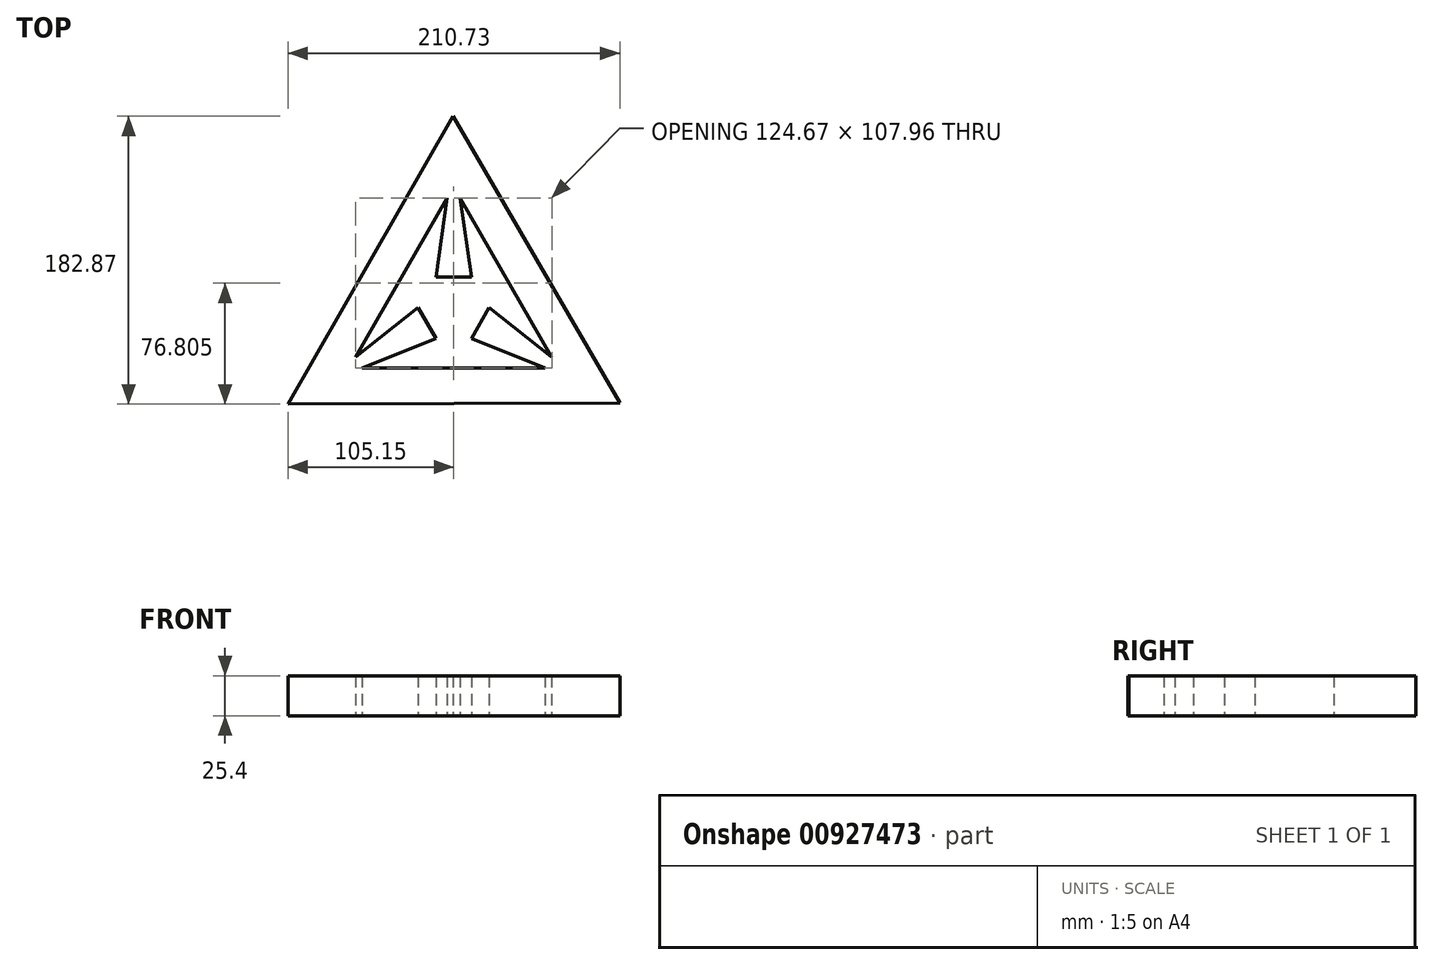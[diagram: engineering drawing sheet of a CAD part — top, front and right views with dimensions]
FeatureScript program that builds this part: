
annotation { "Feature Type Name" : "Feature", "Feature Type Description" : "" }
export const myFeature = defineFeature(function(context is Context, id is Id, definition is map)
    precondition{}
    {
        {
            var Q0;
            Q0=qCreatedBy(makeId("Top.planeOp"),FACE);
            var sketch = newSketch(context, id + "F0", { "sketchPlane" : qUnion([Q0])});
            skCircle(sketch, "E0.cCircle", {"center": v(0, 0) * mm, "radius": 60.83 * mm, "construction": true});
            skLineSegment(sketch, "E0.0", {"start": v(105.58, -60.46) * mm, "end": v(-105.15, -61.2) * mm});
            skLineSegment(sketch, "E0.1", {"start": v(-105.15, -61.2) * mm, "end": v(-0.43, 121.66) * mm});
            skLineSegment(sketch, "E0.2", {"start": v(-0.43, 121.66) * mm, "end": v(105.58, -60.46) * mm});
            skPoint(sketch, "E0.0.midPoint", {"position": v(0.22, -60.83) * mm});
            skPoint(sketch, "E1.0.midPoint", {"position": v(-36.9, -23.18) * mm});
            skCircle(sketch, "E2.cCircle", {"center": v(0, 0) * mm, "radius": 38.39 * mm, "construction": true});
            skLineSegment(sketch, "E2.0", {"start": v(66.49, -38.39) * mm, "end": v(-66.49, -38.39) * mm});
            skLineSegment(sketch, "E2.1", {"start": v(-66.49, -38.39) * mm, "end": v(0, 76.77) * mm});
            skLineSegment(sketch, "E2.2", {"start": v(0, 76.77) * mm, "end": v(66.49, -38.39) * mm});
            skPoint(sketch, "E2.0.midPoint", {"position": v(0, -38.39) * mm});
            skCircle(sketch, "E3.cCircle", {"center": v(0, 0) * mm, "radius": 19.54 * mm, "construction": true});
            skLineSegment(sketch, "E3.0", {"start": v(-11.28, 19.54) * mm, "end": v(11.28, 19.54) * mm});
            skLineSegment(sketch, "E3.1", {"start": v(11.28, 19.54) * mm, "end": v(22.56, 0) * mm});
            skLineSegment(sketch, "E3.2", {"start": v(22.56, 0) * mm, "end": v(11.28, -19.54) * mm});
            skLineSegment(sketch, "E3.3", {"start": v(11.28, -19.54) * mm, "end": v(-11.28, -19.54) * mm});
            skLineSegment(sketch, "E3.4", {"start": v(-11.28, -19.54) * mm, "end": v(-22.56, 0) * mm});
            skLineSegment(sketch, "E3.5", {"start": v(-22.56, 0) * mm, "end": v(-11.28, 19.54) * mm});
            skPoint(sketch, "E3.0.midPoint", {"position": v(0, 19.54) * mm});
            skLineSegment(sketch, "E4", {"start": v(-66.49, -38.39) * mm, "end": v(-33.24, 19.2) * mm});
            skLineSegment(sketch, "E5", {"start": v(-33.24, 19.2) * mm, "end": v(-66.49, -38.39) * mm});
            skLineSegment(sketch, "E6", {"start": v(-49.87, -9.6) * mm, "end": v(-66.49, -38.39) * mm});
            skLineSegment(sketch, "E7", {"start": v(-66.49, -38.39) * mm, "end": v(-58.18, -24) * mm});
            skLineSegment(sketch, "E8", {"start": v(-58.18, -24) * mm, "end": v(-66.49, -38.39) * mm});
            skLineSegment(sketch, "E9", {"start": v(-66.49, -38.39) * mm, "end": v(-62.33, -31.19) * mm});
            skLineSegment(sketch, "E10", {"start": v(0, -38.39) * mm, "end": v(-66.49, -38.39) * mm});
            skLineSegment(sketch, "E11", {"start": v(-66.49, -38.39) * mm, "end": v(-33.24, -38.39) * mm});
            skLineSegment(sketch, "E12", {"start": v(-66.49, -38.39) * mm, "end": v(-49.87, -38.39) * mm});
            skLineSegment(sketch, "E13", {"start": v(-49.87, -38.39) * mm, "end": v(-58.18, -38.39) * mm});
            skLineSegment(sketch, "E14", {"start": v(-58.18, -38.39) * mm, "end": v(-11.28, -19.54) * mm});
            skLineSegment(sketch, "E15", {"start": v(-62.33, -31.19) * mm, "end": v(-22.56, 0) * mm});
            skLineSegment(sketch, "E16", {"start": v(66.49, -38.39) * mm, "end": v(0, -38.39) * mm});
            skLineSegment(sketch, "E17", {"start": v(0, -38.39) * mm, "end": v(33.24, -38.39) * mm});
            skLineSegment(sketch, "E18", {"start": v(66.49, -38.39) * mm, "end": v(33.24, -38.39) * mm});
            skLineSegment(sketch, "E19", {"start": v(66.49, -38.39) * mm, "end": v(49.87, -38.39) * mm});
            skLineSegment(sketch, "E20", {"start": v(49.87, -38.39) * mm, "end": v(66.49, -38.39) * mm});
            skLineSegment(sketch, "E21", {"start": v(66.49, -38.39) * mm, "end": v(33.24, 19.2) * mm});
            skLineSegment(sketch, "E22", {"start": v(33.24, 19.2) * mm, "end": v(49.87, -9.6) * mm});
            skLineSegment(sketch, "E23", {"start": v(66.49, -38.39) * mm, "end": v(49.87, -9.6) * mm});
            skLineSegment(sketch, "E24", {"start": v(49.87, -9.6) * mm, "end": v(58.18, -24) * mm});
            skLineSegment(sketch, "E25", {"start": v(33.24, 19.2) * mm, "end": v(0, 76.77) * mm});
            skLineSegment(sketch, "E26", {"start": v(33.24, 19.2) * mm, "end": v(16.62, 47.98) * mm});
            skLineSegment(sketch, "E27", {"start": v(0, 76.77) * mm, "end": v(16.62, 47.98) * mm});
            skLineSegment(sketch, "E28", {"start": v(8.31, 62.38) * mm, "end": v(0, 76.77) * mm});
            skLineSegment(sketch, "E29", {"start": v(0, 76.77) * mm, "end": v(-33.24, 19.2) * mm});
            skLineSegment(sketch, "E30", {"start": v(-33.24, 19.2) * mm, "end": v(-16.62, 47.98) * mm});
            skLineSegment(sketch, "E31", {"start": v(0, 76.77) * mm, "end": v(-16.62, 47.98) * mm});
            skLineSegment(sketch, "E32", {"start": v(-16.62, 47.98) * mm, "end": v(-8.31, 62.38) * mm});
            skLineSegment(sketch, "E33", {"start": v(0, 76.77) * mm, "end": v(-8.31, 62.38) * mm});
            skLineSegment(sketch, "E34", {"start": v(-4.16, 69.58) * mm, "end": v(-11.28, 19.54) * mm});
            skLineSegment(sketch, "E35", {"start": v(4.16, 69.58) * mm, "end": v(11.28, 19.54) * mm});
            skLineSegment(sketch, "E36", {"start": v(58.18, -24) * mm, "end": v(66.49, -38.39) * mm});
            skLineSegment(sketch, "E37", {"start": v(22.56, 0) * mm, "end": v(62.33, -31.19) * mm});
            skLineSegment(sketch, "E38", {"start": v(62.33, -31.19) * mm, "end": v(22.56, 0) * mm});
            skLineSegment(sketch, "E39", {"start": v(11.28, -19.54) * mm, "end": v(58.18, -38.39) * mm});
            skLineSegment(sketch, "E40", {"start": v(0, 0) * mm, "end": v(0, 19.54) * mm});
            skSolve(sketch);
        }
        {
            var Q0;
            Q0=makeQuery(id+"F0.imprint","IMPRINT",FACE,{"disambiguationData":[TD([[makeQuery(id+"F0.imprint","IMPRINT",EDGE,{"derivedFrom":sQuery(id+"F0.wireOp",EDGE,"E0.0")}),-1.0]])]});
            var Q1;
            Q1=makeQuery(id+"F0.imprint","IMPRINT",FACE,{"disambiguationData":[TD([[makeQuery(id+"F0.imprint","IMPRINT",EDGE,{"derivedFrom":sQuery(id+"F0.wireOp",EDGE,"E3.4")}),1.0]])]});
            var Q2;
            {var subQ2=sQuery(id+"F0.wireOp",EDGE,"E34");Q2=makeQuery(id+"F0.imprint","IMPRINT",FACE,{"disambiguationData":[TD([[makeQuery(id+"F0.imprint","IMPRINT",EDGE,{"derivedFrom":subQ2}),1.0]])]});}
            var Q3;
            Q3=makeQuery(id+"F0.imprint","IMPRINT",FACE,{"disambiguationData":[TD([[makeQuery(id+"F0.imprint","IMPRINT",EDGE,{"derivedFrom":sQuery(id+"F0.wireOp",EDGE,"E3.2")}),1.0]])]});
            extrude(context, id + "F1", {"entities" : qUnion([Q0, Q1, Q2, Q3]), "depth" : 25.4 * mm, "offsetDistance" : 25.4 * mm});
        }
    });
